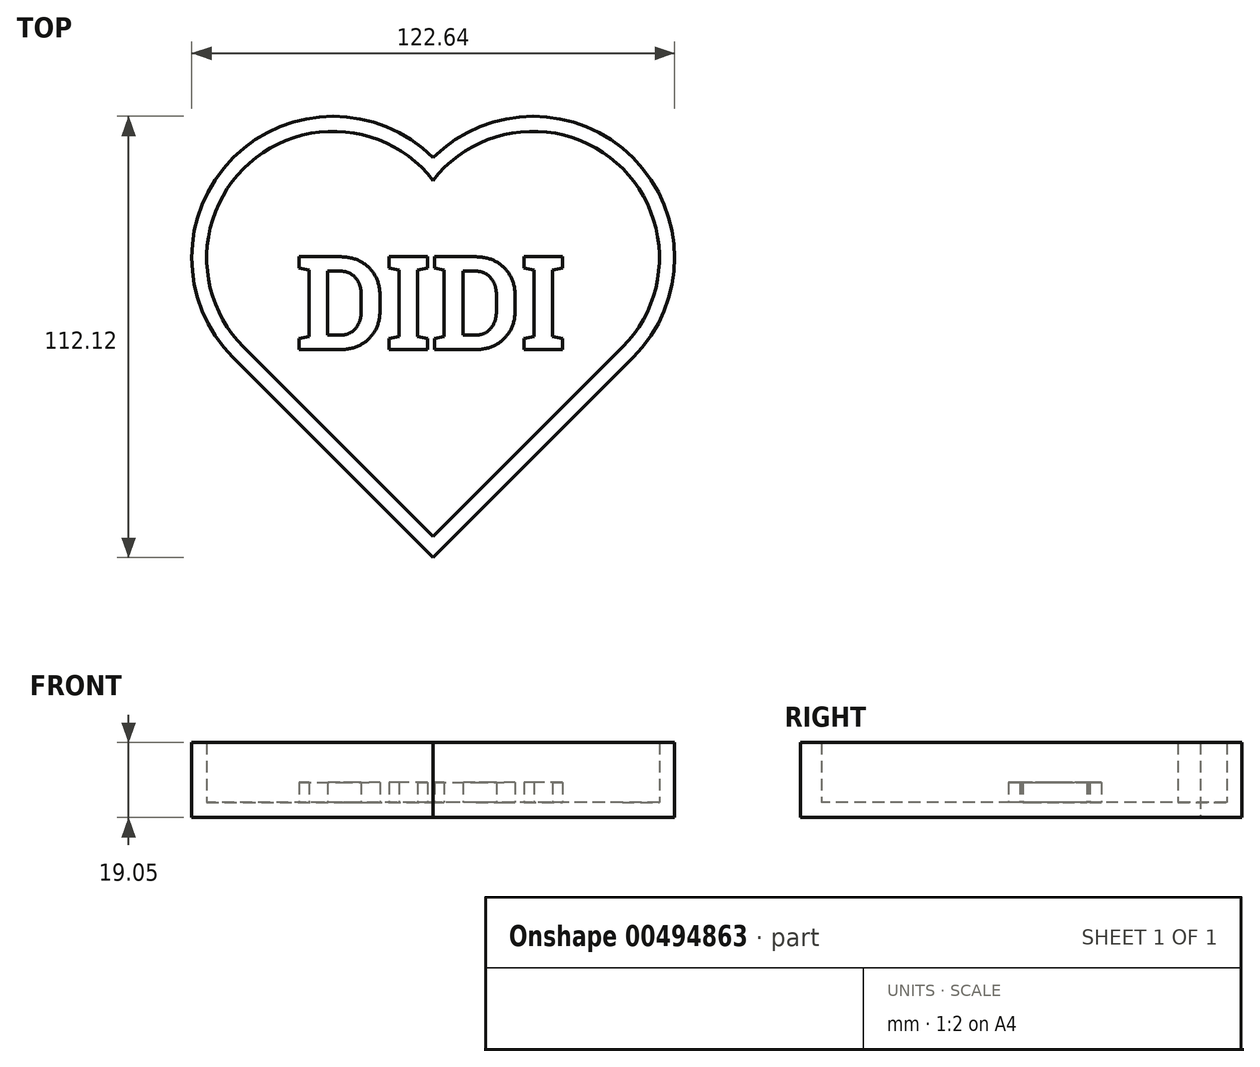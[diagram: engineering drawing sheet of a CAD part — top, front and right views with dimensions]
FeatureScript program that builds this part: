
annotation { "Feature Type Name" : "Feature", "Feature Type Description" : "" }
export const myFeature = defineFeature(function(context is Context, id is Id, definition is map)
    precondition{}
    {
        {
            var Q0;
            Q0=qCreatedBy(makeId("Top.planeOp"),FACE);
            var sketch = newSketch(context, id + "F0", { "sketchPlane" : qUnion([Q0])});
            skLineSegment(sketch, "E0", {"start": v(0, 50.8) * mm, "end": v(0, 0) * mm, "construction": true});
            skLineSegment(sketch, "E1", {"start": v(0, 0) * mm, "end": v(50.8, 0) * mm, "construction": true});
            skLineSegment(sketch, "E2", {"start": v(0, 0) * mm, "end": v(0, -50.8) * mm, "construction": true});
            skLineSegment(sketch, "E3", {"start": v(0, 0) * mm, "end": v(-50.8, 0) * mm, "construction": true});
            skLineSegment(sketch, "E4", {"start": v(-50.8, 0) * mm, "end": v(0, -50.8) * mm});
            skLineSegment(sketch, "E5", {"start": v(50.8, 0) * mm, "end": v(0, -50.8) * mm});
            skArc(sketch, "E6", {"start": v(0, 50.8) * mm, "mid": v(-50.8, 50.8) * mm, "end": v(-50.8, 0) * mm});
            skArc(sketch, "E7", {"start": v(50.8, 0) * mm, "mid": v(50.8, 50.8) * mm, "end": v(0, 50.8) * mm});
            skSolve(sketch);
        }
        {
            var Q0;
            Q0=makeQuery(id+"F0.imprint","IMPRINT",FACE,{"disambiguationData":[TD([[makeQuery(id+"F0.imprint","IMPRINT",EDGE,{"derivedFrom":sQuery(id+"F0.wireOp",EDGE,"E4")}),1.0]])]});
            extrude(context, id + "F1", {"entities" : qUnion([Q0]), "offsetDistance" : 25.4 * mm, "depth" : 19.05 * mm});
        }
        {
            var Q0;
            Q0=makeQuery(id+"F1.opExtrude","CAP_FACE",FACE,{"disambiguationData":[OSD([sQuery(id+"F0.wireOp",EDGE,"E4"),sQuery(id+"F0.wireOp",EDGE,"E5"),sQuery(id+"F0.wireOp",EDGE,"E6"),sQuery(id+"F0.wireOp",EDGE,"E7")])],"isStart":false});
            shell(context, id + "F2", {"entities" : qUnion([Q0]), "thickness" : 3.8 * mm});
        }
        {
            var Q0;
            Q0=makeQuery(id+"F2.opShell","OFFSET_FACE",FACE,{"disambiguationData":[OSD([sQuery(id+"F0.wireOp",EDGE,"E4"),sQuery(id+"F0.wireOp",EDGE,"E5"),sQuery(id+"F0.wireOp",EDGE,"E6"),sQuery(id+"F0.wireOp",EDGE,"E7")])]});
            var sketch = newSketch(context, id + "F3", { "sketchPlane" : qUnion([Q0])});
            skLineSegment(sketch, "E8.bottom", {"start": v(34.93, 25.93) * mm, "end": v(-34.93, 25.93) * mm, "construction": true});
            skLineSegment(sketch, "E8.top", {"start": v(34.93, 2.08) * mm, "end": v(-34.92, 2.08) * mm, "construction": true});
            skLineSegment(sketch, "E8.left", {"start": v(34.92, 25.93) * mm, "end": v(34.92, 2.08) * mm, "construction": true});
            skLineSegment(sketch, "E8.right", {"start": v(-34.93, 25.93) * mm, "end": v(-34.92, 2.08) * mm, "construction": true});
            skPoint(sketch, "E8.middle", {"position": v(0, 14) * mm});
            skText(sketch, "E9", { "text": "DIDI", "fontName": "RobotoSlab-Bold.ttf"});
            const initialGuessF3  = {"E9": [-0.03493, 0.00208, 1, 0, 0.02385]};
            skSetInitialGuess(sketch, initialGuessF3);
            skSolve(sketch);
        }
        {
            var Q0;
            Q0 = qSketchRegion(id + "F3", true);
            extrude(context, id + "F4", {"entities" : qUnion([Q0]), "operationType" : NewBodyOperationType.ADD, "depth" : 5.08 * mm, "offsetDistance" : 25.4 * mm});
        }
    });
